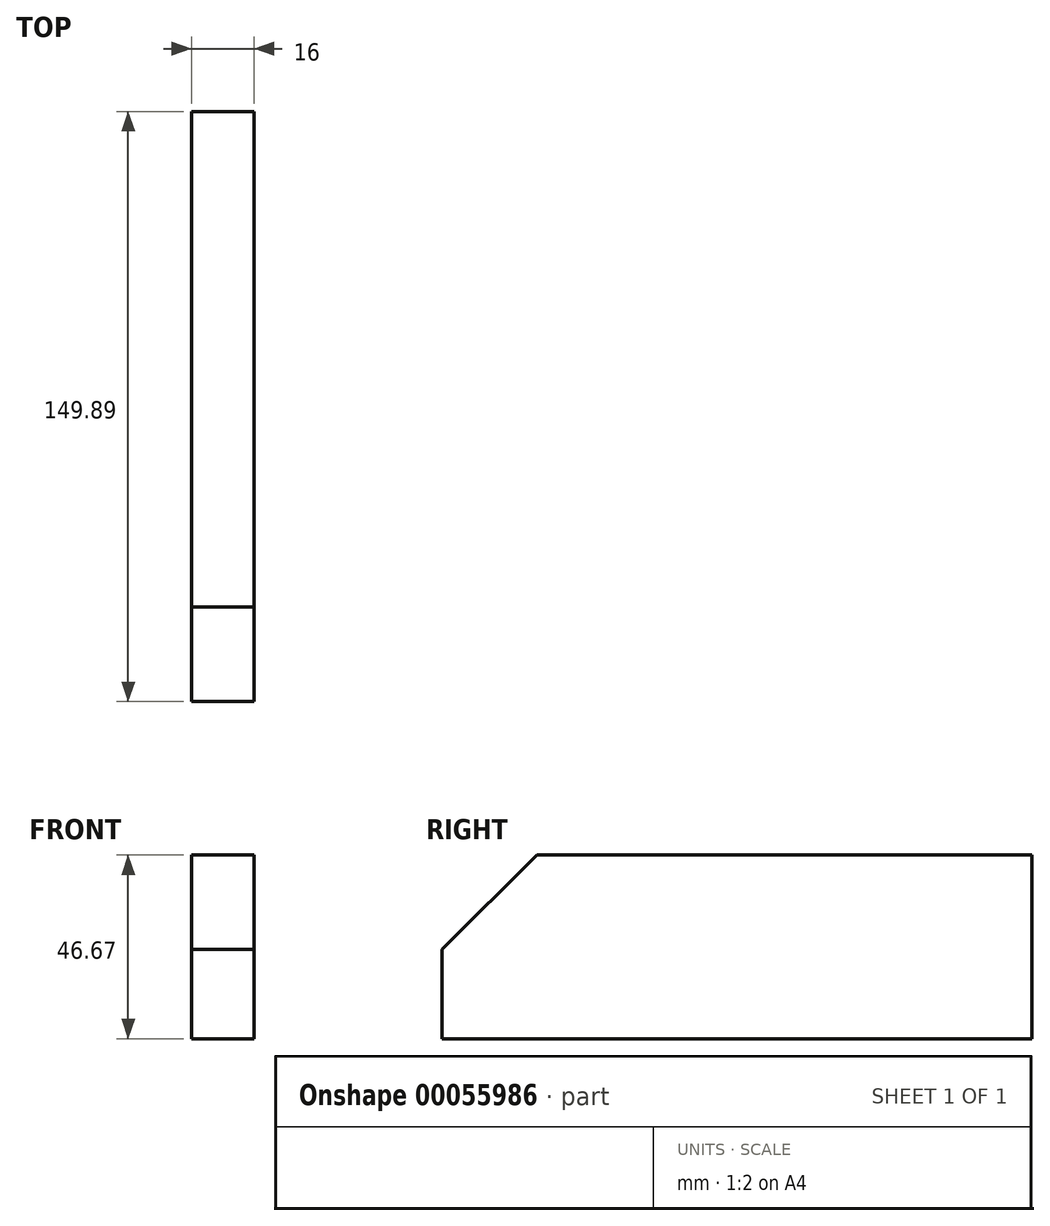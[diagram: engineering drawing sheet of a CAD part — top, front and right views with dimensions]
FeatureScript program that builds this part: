
annotation { "Feature Type Name" : "Feature", "Feature Type Description" : "" }
export const myFeature = defineFeature(function(context is Context, id is Id, definition is map)
    precondition{}
    {
        {
            var Q0;
            Q0=qCreatedBy(makeId("Right.planeOp"),FACE);
            var sketch = newSketch(context, id + "F0", { "sketchPlane" : qUnion([Q0])});
            skLineSegment(sketch, "E0", {"start": v(0, 0) * mm, "end": v(149.89, 0) * mm});
            skLineSegment(sketch, "E1", {"start": v(0, 0) * mm, "end": v(0, 22.63) * mm});
            skLineSegment(sketch, "E2", {"start": v(0, 22.63) * mm, "end": v(24.04, 46.67) * mm});
            skLineSegment(sketch, "E3", {"start": v(149.89, 0) * mm, "end": v(149.89, 46.67) * mm});
            skLineSegment(sketch, "E4", {"start": v(24.04, 46.67) * mm, "end": v(149.89, 46.67) * mm});
            skSolve(sketch);
        }
        {
            var Q0;
            Q0=makeQuery(id+"F0.imprint","IMPRINT",FACE,{"disambiguationData":[TD([[makeQuery(id+"F0.imprint","IMPRINT",EDGE,{"derivedFrom":sQuery(id+"F0.wireOp",EDGE,"E0")}),1.0]])]});
            extrude(context, id + "F1", {"entities" : qUnion([Q0]), "depth" : 16 * mm});
        }
    });
